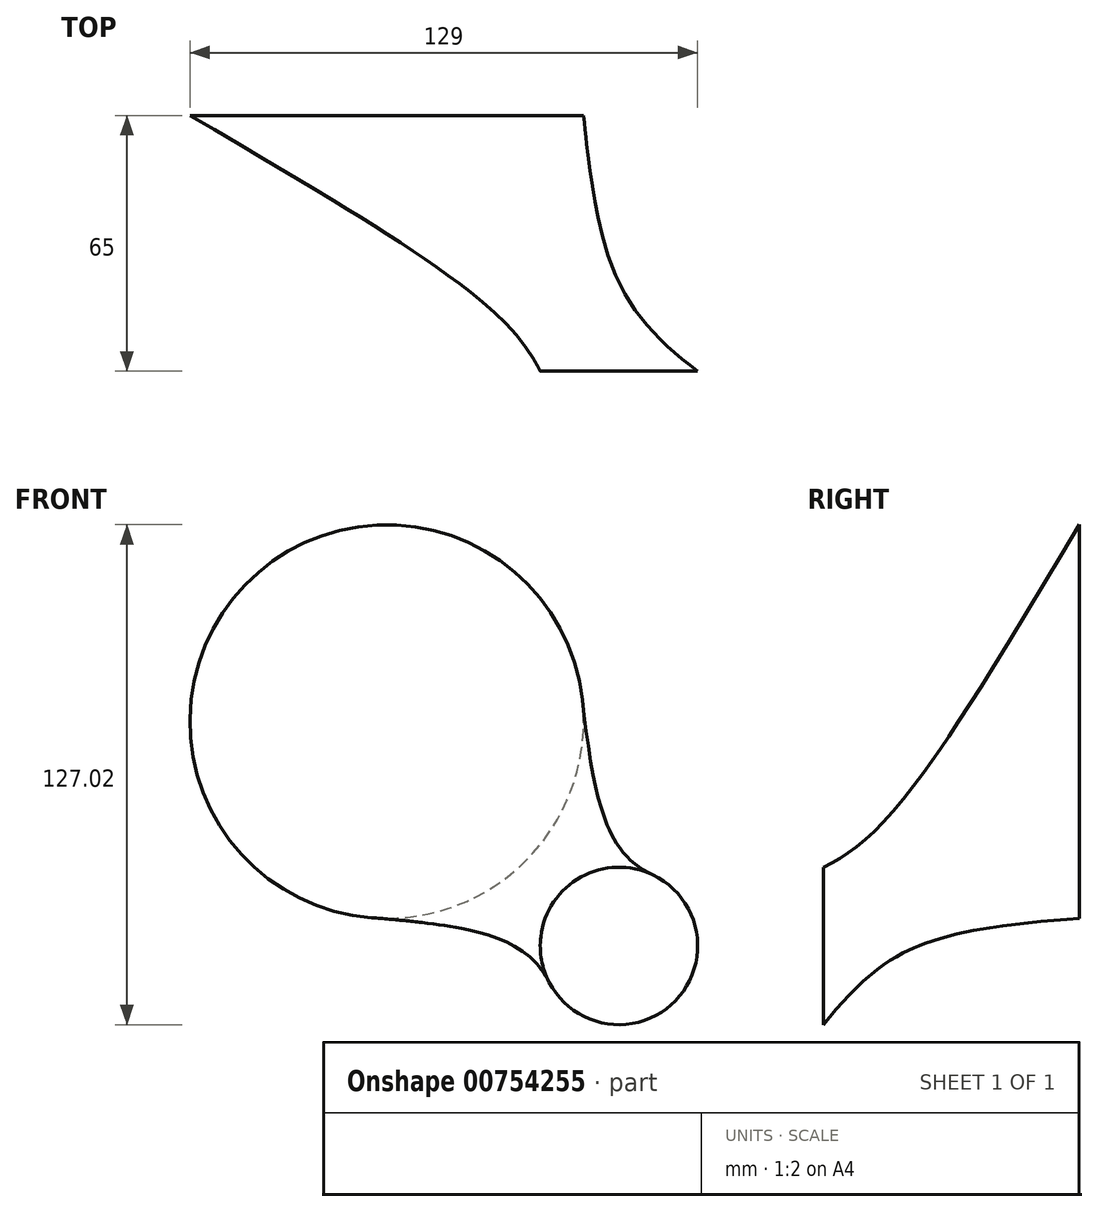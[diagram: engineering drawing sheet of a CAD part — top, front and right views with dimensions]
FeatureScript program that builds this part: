
annotation { "Feature Type Name" : "Feature", "Feature Type Description" : "" }
export const myFeature = defineFeature(function(context is Context, id is Id, definition is map)
    precondition{}
    {
        {
            var Q0;
            Q0=qCreatedBy(makeId("Front.planeOp"),FACE);
            var sketch = newSketch(context, id + "F0", { "sketchPlane" : qUnion([Q0])});
            skCircle(sketch, "E0", {"center": v(0, 0) * mm, "radius": 50 * mm});
            skSolve(sketch);
        }
        {
            var Q0;
            Q0=qCreatedBy(makeId("Front.planeOp"),FACE);
            cPlane(context, id + "F1", {"entities" : qUnion([Q0]), "cplaneType" : CPlaneType.OFFSET, "offset" : 65 * mm, "width" : 150 * mm, "height" : 150 * mm});
        }
        {
            var Q0;
            Q0=qCreatedBy(id+"F1.planeOp",FACE);
            var sketch = newSketch(context, id + "F2", { "sketchPlane" : qUnion([Q0])});
            skCircle(sketch, "E1", {"center": v(59, -57.02) * mm, "radius": 20 * mm});
            skSolve(sketch);
        }
        {
            var Q0;
            Q0=makeQuery(id+"F0.imprint","IMPRINT",FACE,{"disambiguationData":[TD([[makeQuery(id+"F0.imprint","IMPRINT",EDGE,{"derivedFrom":sQuery(id+"F0.wireOp",EDGE,"E0")}),1.0]])]});
            var Q1;
            Q1=makeQuery(id+"F2.imprint","IMPRINT",FACE,{"disambiguationData":[TD([[makeQuery(id+"F2.imprint","IMPRINT",EDGE,{"derivedFrom":sQuery(id+"F2.wireOp",EDGE,"E1")}),1.0]])]});
            loft(context, id + "F3", {"sheetProfilesArray" : [{ "sheetProfileEntities" : qUnion([Q0]) }, { "sheetProfileEntities" : qUnion([Q1]) }]});
        }
    });
